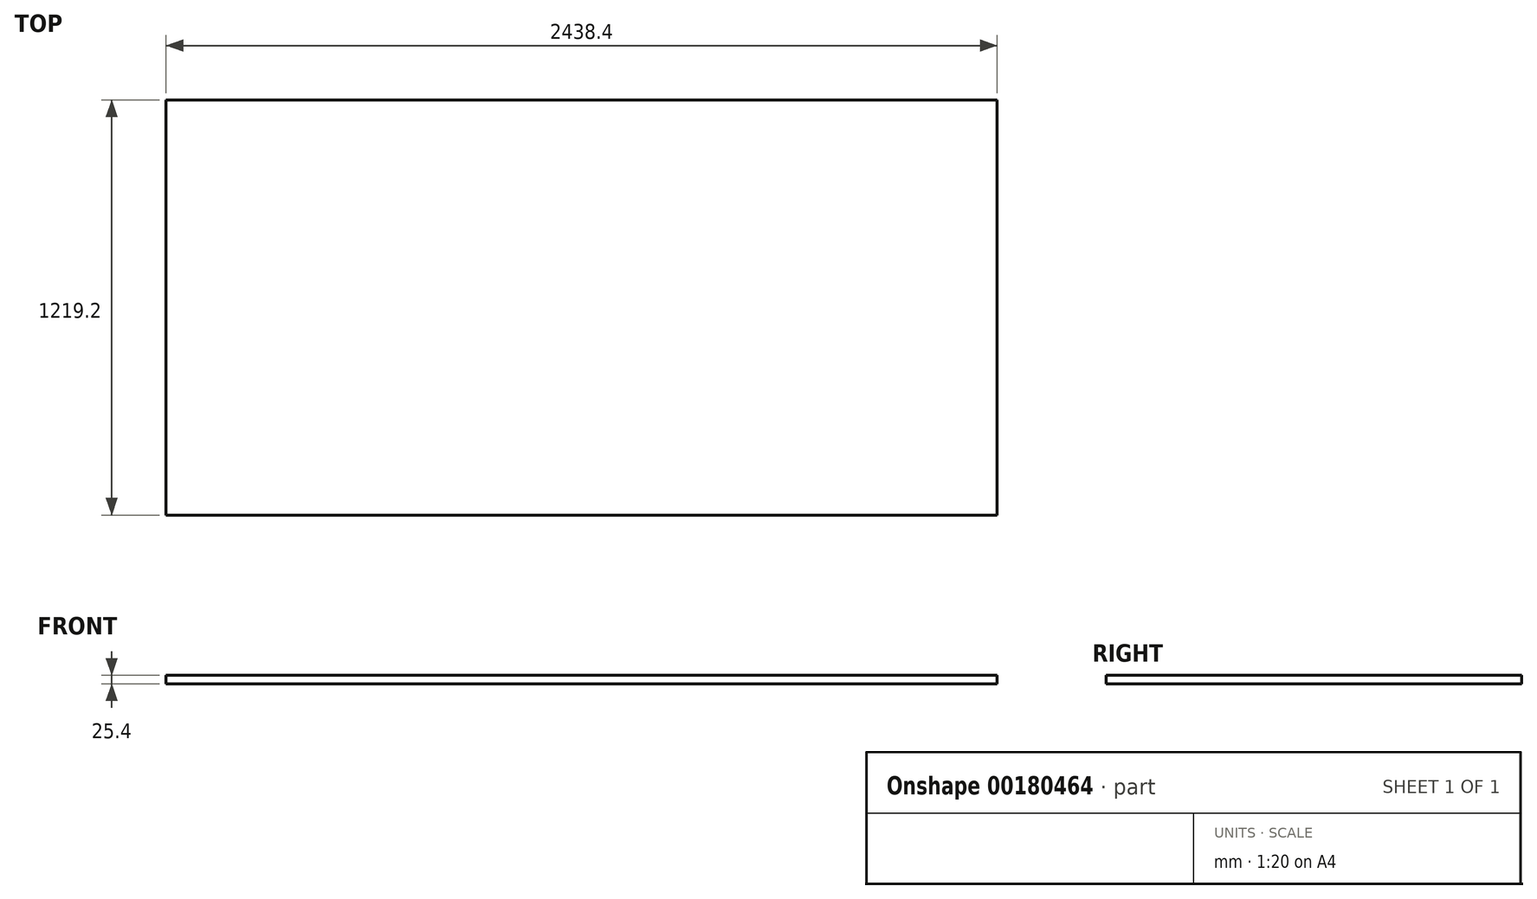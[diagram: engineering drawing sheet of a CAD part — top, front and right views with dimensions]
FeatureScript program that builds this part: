
annotation { "Feature Type Name" : "Feature", "Feature Type Description" : "" }
export const myFeature = defineFeature(function(context is Context, id is Id, definition is map)
    precondition{}
    {
        {
            var Q0;
            Q0=qCreatedBy(makeId("Top.planeOp"),FACE);
            var sketch = newSketch(context, id + "F0", { "sketchPlane" : qUnion([Q0])});
            skLineSegment(sketch, "E0.bottom", {"start": v(-2350.44, 1180.57) * mm, "end": v(87.96, 1180.57) * mm});
            skLineSegment(sketch, "E0.top", {"start": v(-2350.44, -38.63) * mm, "end": v(87.96, -38.63) * mm});
            skLineSegment(sketch, "E0.left", {"start": v(-2350.44, 1180.57) * mm, "end": v(-2350.44, -38.63) * mm});
            skLineSegment(sketch, "E0.right", {"start": v(87.96, 1180.57) * mm, "end": v(87.96, -38.63) * mm});
            skLineSegment(sketch, "E1.bottom", {"start": v(-1156.64, -38.63) * mm, "end": v(-1105.84, -38.63) * mm});
            skLineSegment(sketch, "E1.top", {"start": v(-1156.64, -1994.43) * mm, "end": v(-1105.84, -1994.43) * mm});
            skLineSegment(sketch, "E1.left", {"start": v(-1156.64, -38.63) * mm, "end": v(-1156.64, -1994.43) * mm});
            skLineSegment(sketch, "E1.right", {"start": v(-1105.84, -38.63) * mm, "end": v(-1105.84, -1994.43) * mm});
            skPoint(sketch, "E2", {"position": v(-1131.24, -38.63) * mm});
            skCircle(sketch, "E3", {"center": v(-1131.24, -1969.03) * mm, "radius": 12.7 * mm});
            skPoint(sketch, "E3.centerSnap0", {"position": v(-1131.24, -1994.43) * mm});
            skCircle(sketch, "E4", {"center": v(-1131.24, -1461.03) * mm, "radius": 12.7 * mm});
            skSolve(sketch);
        }
        {
            var Q0;
            Q0=makeQuery(id+"F0.imprint","IMPRINT",FACE,{"disambiguationData":[TD([[makeQuery(id+"F0.imprint","IMPRINT",EDGE,{"derivedFrom":sQuery(id+"F0.wireOp",EDGE,"E0.bottom")}),-1.0]])]});
            var Q1;
            Q1=makeQuery(id+"F0.imprint","IMPRINT",FACE,{"disambiguationData":[TD([[makeQuery(id+"F0.imprint","IMPRINT",EDGE,{"derivedFrom":sQuery(id+"F0.wireOp",EDGE,"E1.bottom")}),-1.0]])]});
            extrude(context, id + "F1", {"entities" : qUnion([Q0, Q1]), "depth" : 25.4 * mm, "offsetDistance" : 25.4 * mm});
        }
    });
